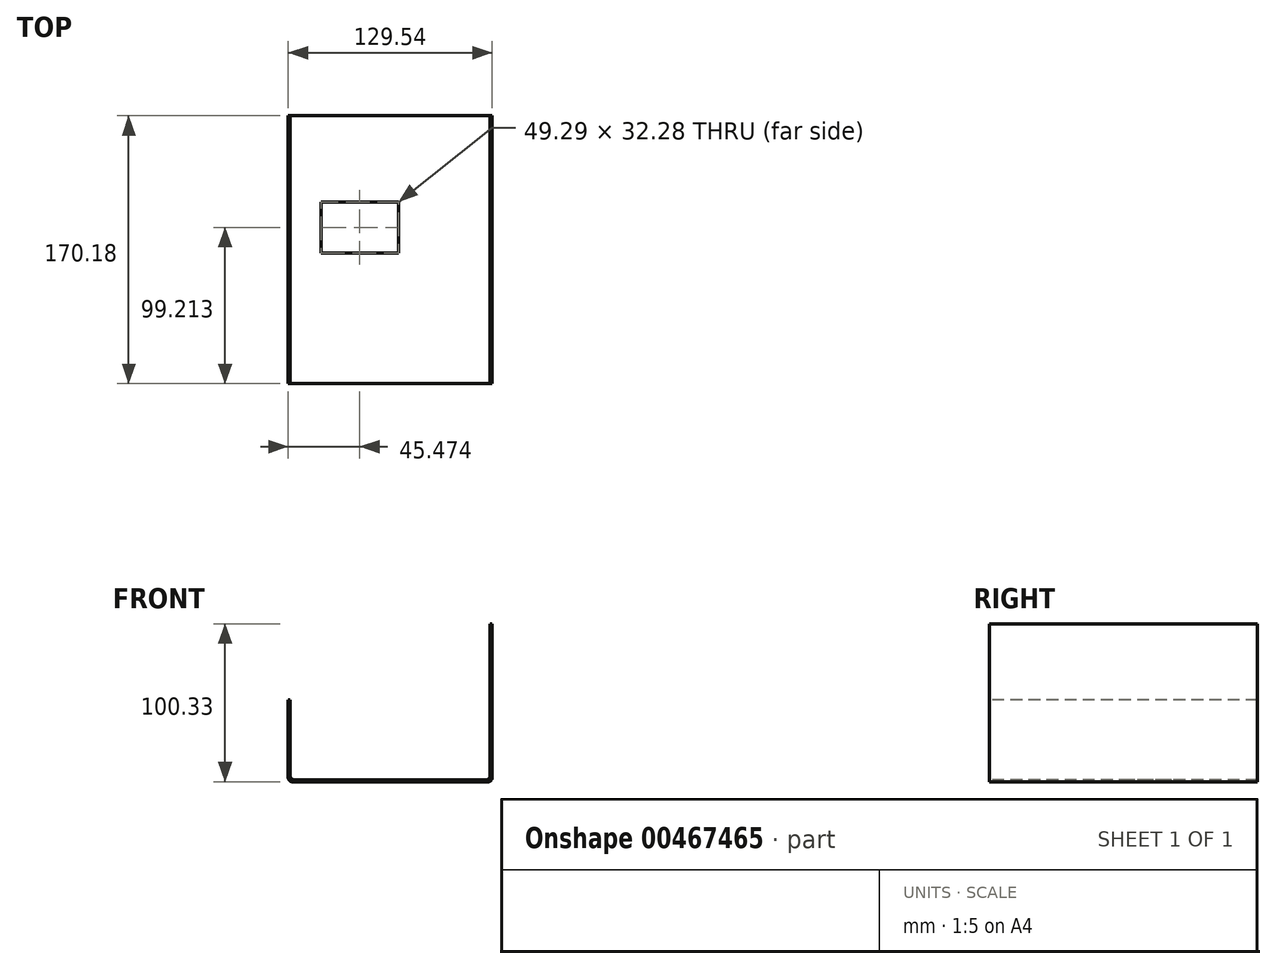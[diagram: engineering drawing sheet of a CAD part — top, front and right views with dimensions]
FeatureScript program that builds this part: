
annotation { "Feature Type Name" : "Feature", "Feature Type Description" : "" }
export const myFeature = defineFeature(function(context is Context, id is Id, definition is map)
    precondition{}
    {
        {
            var Q0;
            Q0=qCreatedBy(makeId("Front.planeOp"),FACE);
            var sketch = newSketch(context, id + "F0", { "sketchPlane" : qUnion([Q0])});
            skLineSegment(sketch, "E0", {"start": v(0, 0) * mm, "end": v(114.47, 0) * mm});
            skLineSegment(sketch, "E1", {"start": v(117.01, 2.54) * mm, "end": v(117.01, 100.33) * mm});
            skLineSegment(sketch, "E2", {"start": v(117.01, 100.33) * mm, "end": v(115.74, 100.33) * mm});
            skLineSegment(sketch, "E3", {"start": v(115.74, 100.33) * mm, "end": v(115.74, 3.81) * mm});
            skLineSegment(sketch, "E4", {"start": v(113.2, 1.27) * mm, "end": v(-8.72, 1.27) * mm});
            skLineSegment(sketch, "E5", {"start": v(-11.26, 3.81) * mm, "end": v(-11.26, 52.07) * mm});
            skLineSegment(sketch, "E6", {"start": v(-11.26, 52.07) * mm, "end": v(-12.53, 52.07) * mm});
            skLineSegment(sketch, "E7", {"start": v(-12.53, 52.07) * mm, "end": v(-12.53, 2.54) * mm});
            skLineSegment(sketch, "E8", {"start": v(-9.99, 0) * mm, "end": v(0, 0) * mm});
            skPoint(sketch, "E9.visualSharp", {"position": v(115.74, 1.27) * mm});
            skArc(sketch, "E9.filletArc", {"start": v(113.2, 1.27) * mm, "mid": v(115, 2.01) * mm, "end": v(115.74, 3.81) * mm});
            skPoint(sketch, "E10.visualSharp", {"position": v(117.01, 0) * mm});
            skArc(sketch, "E10.filletArc", {"start": v(114.47, 0) * mm, "mid": v(116.27, 0.74) * mm, "end": v(117.01, 2.54) * mm});
            skPoint(sketch, "E11.visualSharp", {"position": v(-11.26, 1.27) * mm});
            skArc(sketch, "E11.filletArc", {"start": v(-11.26, 3.81) * mm, "mid": v(-10.51, 2.01) * mm, "end": v(-8.72, 1.27) * mm});
            skPoint(sketch, "E12.visualSharp", {"position": v(-12.53, 0) * mm});
            skArc(sketch, "E12.filletArc", {"start": v(-12.53, 2.54) * mm, "mid": v(-11.78, 0.74) * mm, "end": v(-9.99, 0) * mm});
            skSolve(sketch);
        }
        {
            var Q0;
            Q0=makeQuery(id+"F0.imprint","IMPRINT",FACE,{"disambiguationData":[TD([[makeQuery(id+"F0.imprint","IMPRINT",EDGE,{"derivedFrom":sQuery(id+"F0.wireOp",EDGE,"E0")}),1.0]])]});
            extrude(context, id + "F1", {"entities" : qUnion([Q0]), "oppositeDirection" : true, "depth" : 170.18 * mm});
        }
        {
            var Q0;
            Q0=makeQuery(id+"F1.opExtrude","SWEPT_FACE",FACE,{"disambiguationData":[OSD([sQuery(id+"F0.wireOp",EDGE,"E4")])]});
            var sketch = newSketch(context, id + "F2", { "sketchPlane" : qUnion([Q0])});
            skLineSegment(sketch, "E13.bottom", {"start": v(8.3, 115.35) * mm, "end": v(57.59, 115.35) * mm});
            skLineSegment(sketch, "E13.top", {"start": v(8.3, 83.07) * mm, "end": v(57.59, 83.07) * mm});
            skLineSegment(sketch, "E13.left", {"start": v(8.3, 115.35) * mm, "end": v(8.3, 83.07) * mm});
            skLineSegment(sketch, "E13.right", {"start": v(57.59, 115.35) * mm, "end": v(57.59, 83.07) * mm});
            skSolve(sketch);
        }
        {
            var Q0;
            Q0=qSketchRegion(id+"F2",true);
            extrude(context, id + "F3", {"entities" : qUnion([Q0]), "operationType" : NewBodyOperationType.REMOVE, "oppositeDirection" : true, "depth" : 25.4 * mm});
        }
    });
